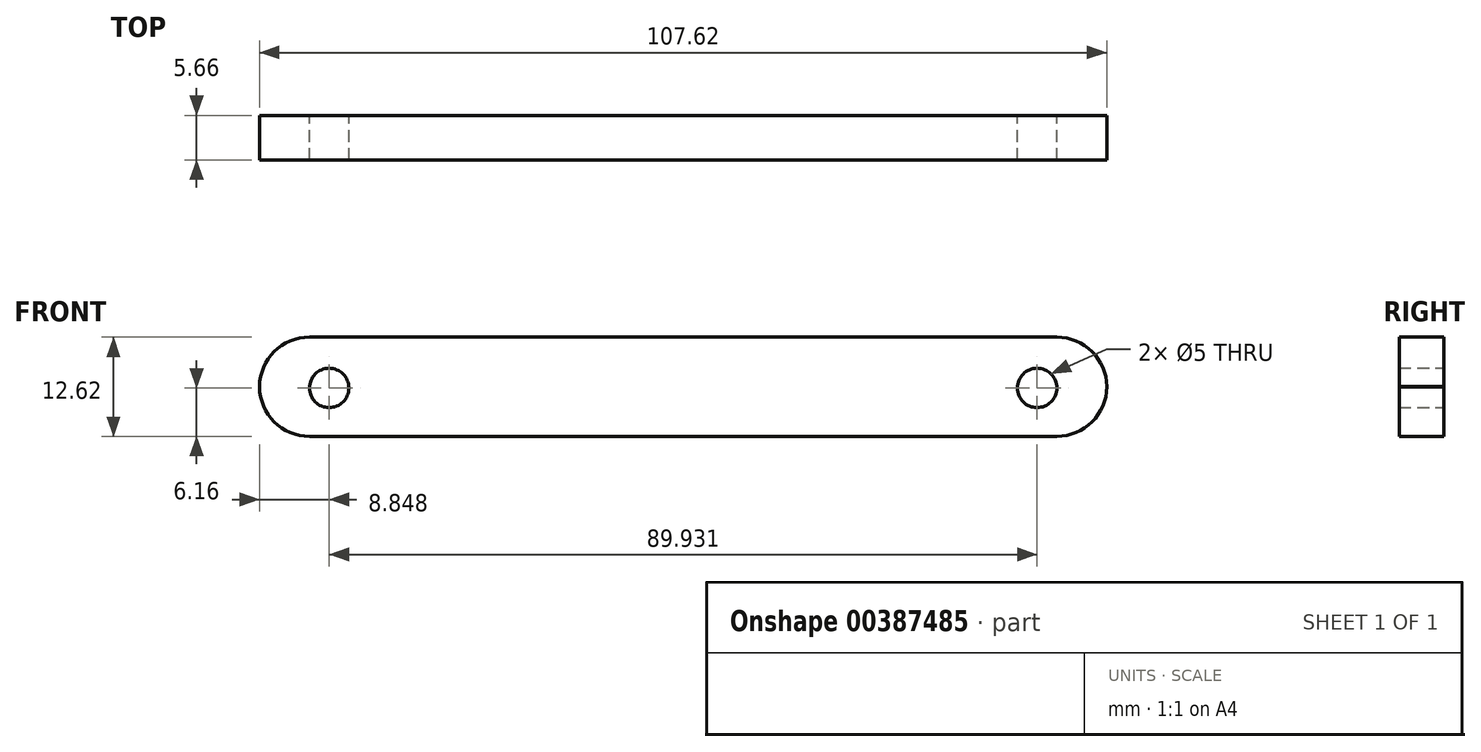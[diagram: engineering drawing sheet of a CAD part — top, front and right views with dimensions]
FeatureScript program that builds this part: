
annotation { "Feature Type Name" : "Feature", "Feature Type Description" : "" }
export const myFeature = defineFeature(function(context is Context, id is Id, definition is map)
    precondition{}
    {
        {
            var Q0;
            Q0=qCreatedBy(makeId("Front.planeOp"),FACE);
            var sketch = newSketch(context, id + "F0", { "sketchPlane" : qUnion([Q0])});
            skLineSegment(sketch, "E0.bottom", {"start": v(-25.32, 6.46) * mm, "end": v(69.6, 6.46) * mm});
            skLineSegment(sketch, "E0.top", {"start": v(-25.32, -6.16) * mm, "end": v(69.6, -6.16) * mm});
            skLineSegment(sketch, "E0.left", {"start": v(-31.67, 0.2) * mm, "end": v(-31.67, 0.11) * mm});
            skLineSegment(sketch, "E0.right", {"start": v(75.95, 0.2) * mm, "end": v(75.95, 0.11) * mm});
            skPoint(sketch, "E1.visualSharp", {"position": v(-31.67, 6.46) * mm});
            skArc(sketch, "E1.filletArc", {"start": v(-25.32, 6.46) * mm, "mid": v(-29.8, 4.6) * mm, "end": v(-31.67, 0.11) * mm});
            skPoint(sketch, "E2.visualSharp", {"position": v(-31.67, -6.16) * mm});
            skArc(sketch, "E2.filletArc", {"start": v(-31.67, 0.2) * mm, "mid": v(-29.8, -4.3) * mm, "end": v(-25.32, -6.16) * mm});
            skPoint(sketch, "E3.visualSharp", {"position": v(75.95, -6.16) * mm});
            skArc(sketch, "E3.filletArc", {"start": v(69.6, -6.16) * mm, "mid": v(74.1, -4.3) * mm, "end": v(75.95, 0.2) * mm});
            skPoint(sketch, "E4.visualSharp", {"position": v(75.95, 6.46) * mm});
            skArc(sketch, "E4.filletArc", {"start": v(75.95, 0.11) * mm, "mid": v(74.1, 4.6) * mm, "end": v(69.6, 6.46) * mm});
            skCircle(sketch, "E5", {"center": v(-22.82, 0) * mm, "radius": 2.5 * mm});
            skCircle(sketch, "E6", {"center": v(67.1, 0) * mm, "radius": 2.5 * mm});
            skSolve(sketch);
        }
        {
            var Q0;
            Q0 = qSketchRegion(id + "F0", true);
            extrude(context, id + "F1", {"entities" : qUnion([Q0]), "depth" : 5.66 * mm});
        }
    });
